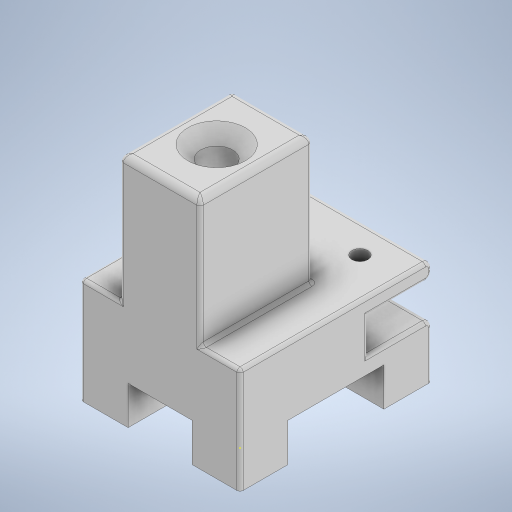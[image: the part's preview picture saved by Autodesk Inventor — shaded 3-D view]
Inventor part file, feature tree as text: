
AUTODESK INVENTOR PART (.ipt)
format: ipt  version: 2024 (Build 280153000, 153)  size: 391,168 bytes
history: native  units: in
note: dims shown in document units (in); Inventor stores cm internally (conversion verified against a paired STEP export)
features: sketch x9, extrude x8, fillet x4, chamfer x1
ambient origin geometry x8: Origin, YZ Plane, XZ Plane, XY Plane, X Axis, Y Axis, Z Axis, Center Point
bodies: Solid1 (feature_tree)
feature tree (22):
  extrude  "Extrusion1"  Depth=2.3622in
  extrude  "Extrusion2"  Depth=1.5748in
  extrude  "Extrusion3"  Depth=0.1969in TaperAngle=0.0deg
  extrude  "Extrusion4"  Depth=0.1969in
  extrude  "Extrusion5"  Depth=1.378in
  extrude  "Extrusion6"  Depth=0.3937in
  extrude  "Extrusion7"  Depth=0.3937in TaperAngle=0.0deg
  chamfer  "Chamfer1"  Distance=0.0787in Angle=45.0deg
  sketch  "Sketch8"  dims[d24=0.5906in d25=0.5906in d26=0.5906in d27=0.5906in d28=0.5906in d29=0.5906in]
  extrude  "Extrusion8"  Depth=0.5906in
  fillet  "Fillet1"  Radius=0.5906in
  fillet  "Fillet2"  Radius=0.5906in
  fillet  "Fillet3"  Radius=0.5906in
  fillet  "Fillet4"  Radius=0.5906in
  sketch  "Sketch1"  dims[d0=1.9685in d1=2.3622in]
  sketch  "Sketch2"  dims[d2=0.1969in d3=0.0in d4=1.5748in]
  sketch  "Sketch3"  dims[d5=0.4331in d6=0.0in d7=0.1969in d8=0.0in]
  sketch  "Sketch4"  dims[d9=0.1969in d10=0.1969in]
  sketch  "Sketch5"  dims[d11=0.1969in d12=0.0in d13=1.378in]
  sketch  "Sketch6"  dims[d14=1.1811in d15=0.0in d16=0.3937in]
  sketch  "Sketch7"  dims[d17=1.1811in d18=0.0in d19=0.3937in d20=0.0in d21=0.1575in d22=0.0787in d23=45.0deg]
  sketch  "Sketch9"  dims[d30=0.4724in d31=0.0in d32=0.0787in d33=0.0394in d34=0.0394in d35=0.0394in]
